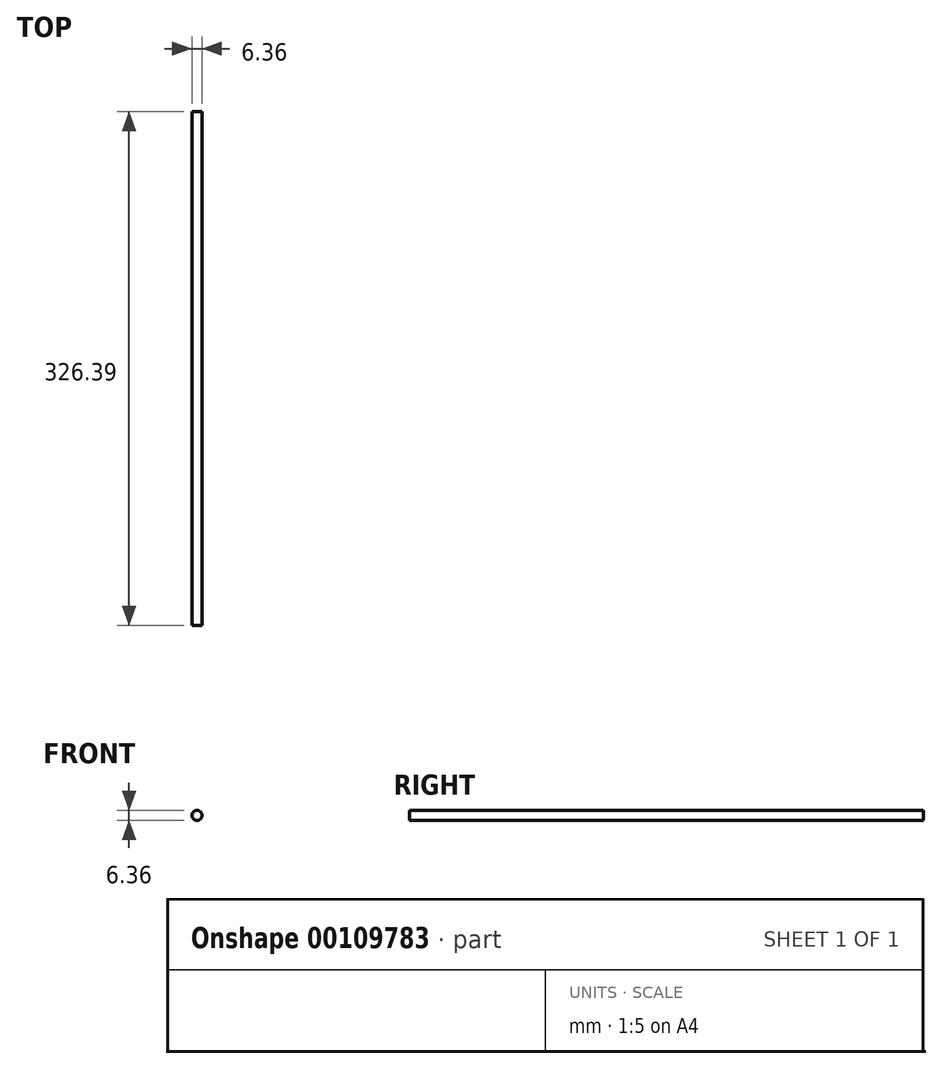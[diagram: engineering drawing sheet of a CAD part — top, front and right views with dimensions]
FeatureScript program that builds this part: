
annotation { "Feature Type Name" : "Feature", "Feature Type Description" : "" }
export const myFeature = defineFeature(function(context is Context, id is Id, definition is map)
    precondition{}
    {
        {
            var Q0;
            Q0=qCreatedBy(makeId("Front.planeOp"),FACE);
            var sketch = newSketch(context, id + "F0", { "sketchPlane" : qUnion([Q0])});
            skCircle(sketch, "E0", {"center": v(0, 0) * mm, "radius": 3.18 * mm});
            skSolve(sketch);
        }
        {
            var Q0;
            Q0 = qSketchRegion(id + "F0", true);
            extrude(context, id + "F1", {"entities" : qUnion([Q0]), "depth" : 326.4 * mm});
        }
    });
